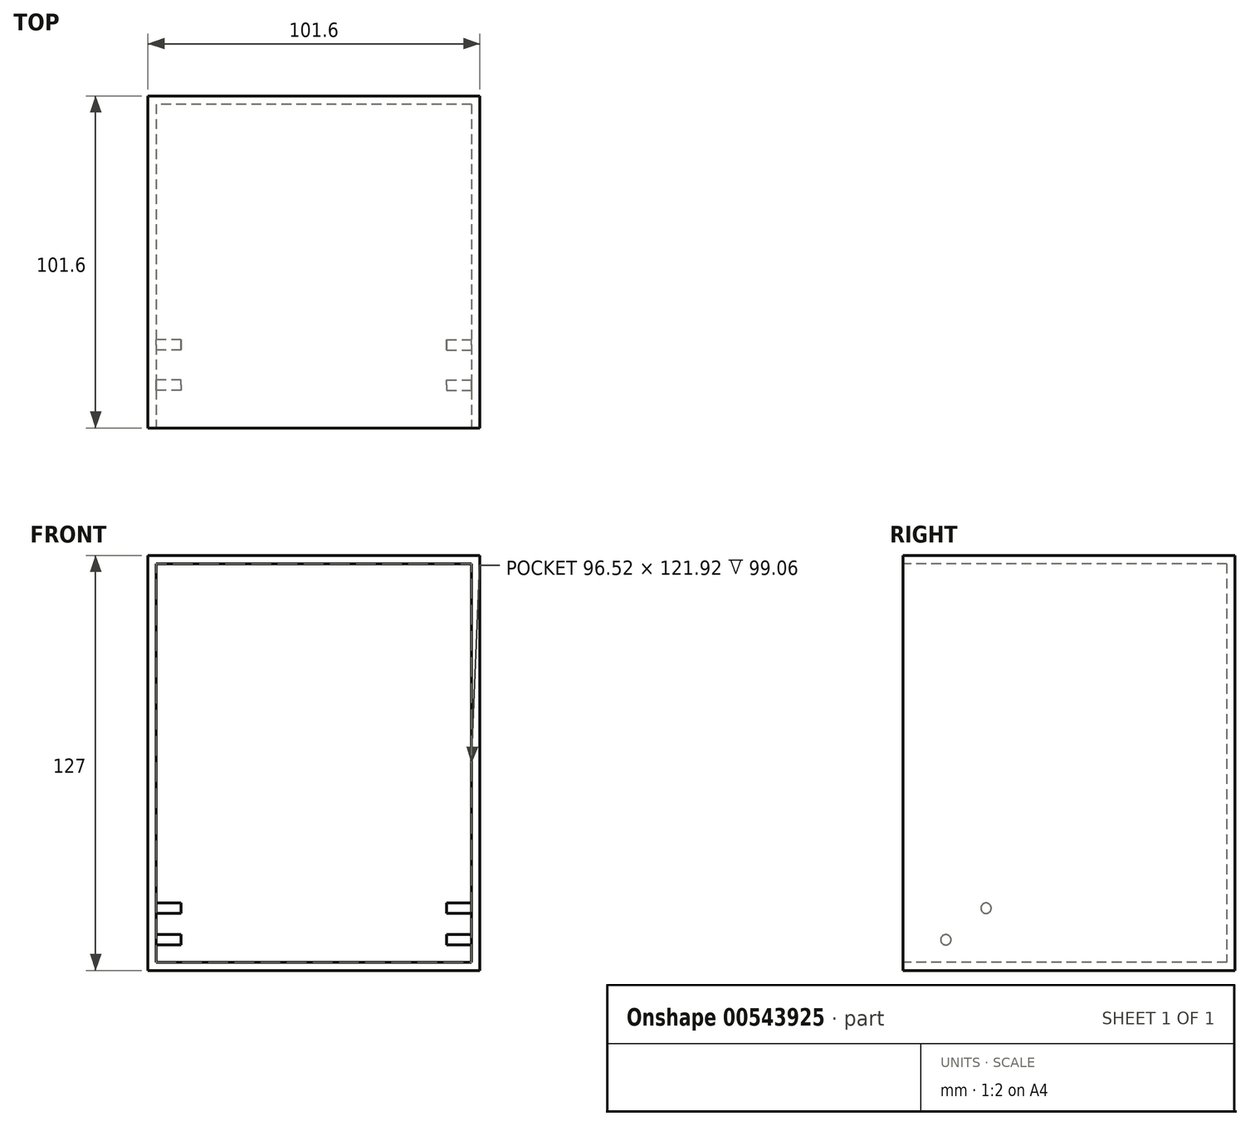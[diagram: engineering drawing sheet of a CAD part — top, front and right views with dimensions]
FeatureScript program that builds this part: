
annotation { "Feature Type Name" : "Feature", "Feature Type Description" : "" }
export const myFeature = defineFeature(function(context is Context, id is Id, definition is map)
    precondition{}
    {
        {
            var Q0;
            Q0=qCreatedBy(makeId("Top.planeOp"),FACE);
            var sketch = newSketch(context, id + "F0", { "sketchPlane" : qUnion([Q0])});
            skLineSegment(sketch, "E0.bottom", {"start": v(50.8, 50.8) * mm, "end": v(-50.8, 50.8) * mm});
            skLineSegment(sketch, "E0.top", {"start": v(50.8, -50.8) * mm, "end": v(-50.8, -50.8) * mm});
            skLineSegment(sketch, "E0.left", {"start": v(50.8, 50.8) * mm, "end": v(50.8, -50.8) * mm});
            skLineSegment(sketch, "E0.right", {"start": v(-50.8, 50.8) * mm, "end": v(-50.8, -50.8) * mm});
            skPoint(sketch, "E0.middle", {"position": v(0, 0) * mm});
            skSolve(sketch);
        }
        {
            var Q0;
            Q0=makeQuery(id+"F0.imprint","IMPRINT",FACE,{"disambiguationData":[TD([[makeQuery(id+"F0.imprint","IMPRINT",EDGE,{"derivedFrom":sQuery(id+"F0.wireOp",EDGE,"E0.bottom")}),1.0]])]});
            extrude(context, id + "F1", {"entities" : qUnion([Q0]), "depth" : 127 * mm, "offsetDistance" : 25.4 * mm});
        }
        {
            var Q0;
            Q0=makeQuery(id+"F1.opExtrude","SWEPT_FACE",FACE,{"disambiguationData":[OSD([sQuery(id+"F0.wireOp",EDGE,"E0.top")])]});
            shell(context, id + "F2", {"entities" : qUnion([Q0]), "thickness" : 2.54 * mm});
        }
        {
            var Q0;
            Q0=makeQuery(id+"F2.opShell","OFFSET_FACE",FACE,{"disambiguationData":[OSD([sQuery(id+"F0.wireOp",EDGE,"E0.left")])]});
            var sketch = newSketch(context, id + "F3", { "sketchPlane" : qUnion([Q0])});
            skLineSegment(sketch, "E1", {"start": v(50.8, 2.54) * mm, "end": v(38.1, 2.54) * mm});
            skLineSegment(sketch, "E2", {"start": v(38.1, 2.54) * mm, "end": v(38.1, 8.9) * mm});
            skSolve(sketch);
        }
        {
            var Q0;
            {var subQ3=sQuery(id+"F3.wireOp",EDGE,"E1");Q0=makeQuery(id+"F3.imprint","IMPRINT",FACE,{"disambiguationData":[TD([[makeQuery(id+"F3.imprint","IMPRINT",EDGE,{"derivedFrom":subQ3}),1.0]])]});}
            var sketch = newSketch(context, id + "F4", { "sketchPlane" : qUnion([Q0])});
            skCircle(sketch, "E3", {"center": v(37.69, 9.37) * mm, "radius": 1.59 * mm});
            skSolve(sketch);
        }
        {
            var Q0;
            Q0 = qSketchRegion(id + "F4", true);
            extrude(context, id + "F5", {"entities" : qUnion([Q0]), "operationType" : NewBodyOperationType.ADD, "depth" : 7.62 * mm, "offsetDistance" : 25.4 * mm});
        }
        {
            var Q0;
            Q0=makeQuery(id+"F1.opExtrude","SWEPT_FACE",FACE,{"disambiguationData":[OSD([sQuery(id+"F0.wireOp",EDGE,"E0.right")])]});
            var sketch = newSketch(context, id + "F6", { "sketchPlane" : qUnion([Q0])});
            skCircle(sketch, "E4", {"center": v(25.12, 12.59) * mm, "radius": 1.59 * mm});
            skSolve(sketch);
        }
        {
            var Q0;
            Q0=makeQuery(id+"F1.opExtrude","SWEPT_BODY",BODY,{"disambiguationData":[OSD([sQuery(id+"F0.wireOp",EDGE,"E0.bottom"),sQuery(id+"F0.wireOp",EDGE,"E0.top"),sQuery(id+"F0.wireOp",EDGE,"E0.left"),sQuery(id+"F0.wireOp",EDGE,"E0.right")])]});
            var Q1;
            Q1=qCreatedBy(makeId("Right.planeOp"),FACE);
            mirror(context, id + "F7", {"operationType" : NewBodyOperationType.ADD, "entities" : qUnion([Q0]), "mirrorPlane" : qUnion([Q1])});
        }
        {
            var Q0;
            Q0=makeQuery(id+"F1.opExtrude","SWEPT_BODY",BODY,{"disambiguationData":[OSD([sQuery(id+"F0.wireOp",EDGE,"E0.bottom"),sQuery(id+"F0.wireOp",EDGE,"E0.top"),sQuery(id+"F0.wireOp",EDGE,"E0.left"),sQuery(id+"F0.wireOp",EDGE,"E0.right")])]});
            var Q1;
            Q1=qCreatedBy(makeId("Right.planeOp"),FACE);
            mirror(context, id + "F8", {"operationType" : NewBodyOperationType.ADD, "entities" : qUnion([Q0]), "mirrorPlane" : qUnion([Q1])});
        }
        {
            var Q0;
            Q0=makeQuery(id+"F6.imprint","IMPRINT",FACE,{"disambiguationData":[TD([[makeQuery(id+"F6.imprint","IMPRINT",EDGE,{"derivedFrom":sQuery(id+"F6.wireOp",EDGE,"E4")}),-1.0]])]});
            var sketch = newSketch(context, id + "F9", { "sketchPlane" : qUnion([Q0])});
            skLineSegment(sketch, "E5", {"start": v(0, 0) * mm, "end": v(25.4, 0) * mm});
            skLineSegment(sketch, "E6", {"start": v(25.4, 0) * mm, "end": v(25.4, 19.05) * mm});
            skCircle(sketch, "E7", {"center": v(25.4, 19.05) * mm, "radius": 1.59 * mm});
            skSolve(sketch);
        }
        {
            var Q0;
            Q0=makeQuery(id+"F6.imprint","IMPRINT",FACE,{"disambiguationData":[TD([[makeQuery(id+"F6.imprint","IMPRINT",EDGE,{"derivedFrom":sQuery(id+"F6.wireOp",EDGE,"E4")}),-1.0]])]});
            var sketch = newSketch(context, id + "F10", { "sketchPlane" : qUnion([Q0])});
            skLineSegment(sketch, "E8", {"start": v(0, 0) * mm, "end": v(25.4, 0) * mm});
            skLineSegment(sketch, "E9", {"start": v(25.4, 0) * mm, "end": v(25.4, 19.05) * mm});
            skLineSegment(sketch, "E10", {"start": v(20.22, 28.07) * mm, "end": v(-55.14, 60.74) * mm});
            skCircle(sketch, "E11", {"center": v(25.4, 19.05) * mm, "radius": 1.59 * mm});
            skSolve(sketch);
        }
        {
            var Q0;
            Q0 = qSketchRegion(id + "F10", true);
            extrude(context, id + "F11", {"entities" : qUnion([Q0]), "operationType" : NewBodyOperationType.ADD, "oppositeDirection" : true, "depth" : 10.16 * mm, "offsetDistance" : 25.4 * mm});
        }
        {
            var Q0;
            Q0=makeQuery(id+"F1.opExtrude","SWEPT_BODY",BODY,{"disambiguationData":[OSD([sQuery(id+"F0.wireOp",EDGE,"E0.bottom"),sQuery(id+"F0.wireOp",EDGE,"E0.top"),sQuery(id+"F0.wireOp",EDGE,"E0.left"),sQuery(id+"F0.wireOp",EDGE,"E0.right")])]});
            var Q1;
            Q1=qCreatedBy(makeId("Right.planeOp"),FACE);
            mirror(context, id + "F12", {"operationType" : NewBodyOperationType.ADD, "entities" : qUnion([Q0]), "mirrorPlane" : qUnion([Q1])});
        }
    });
